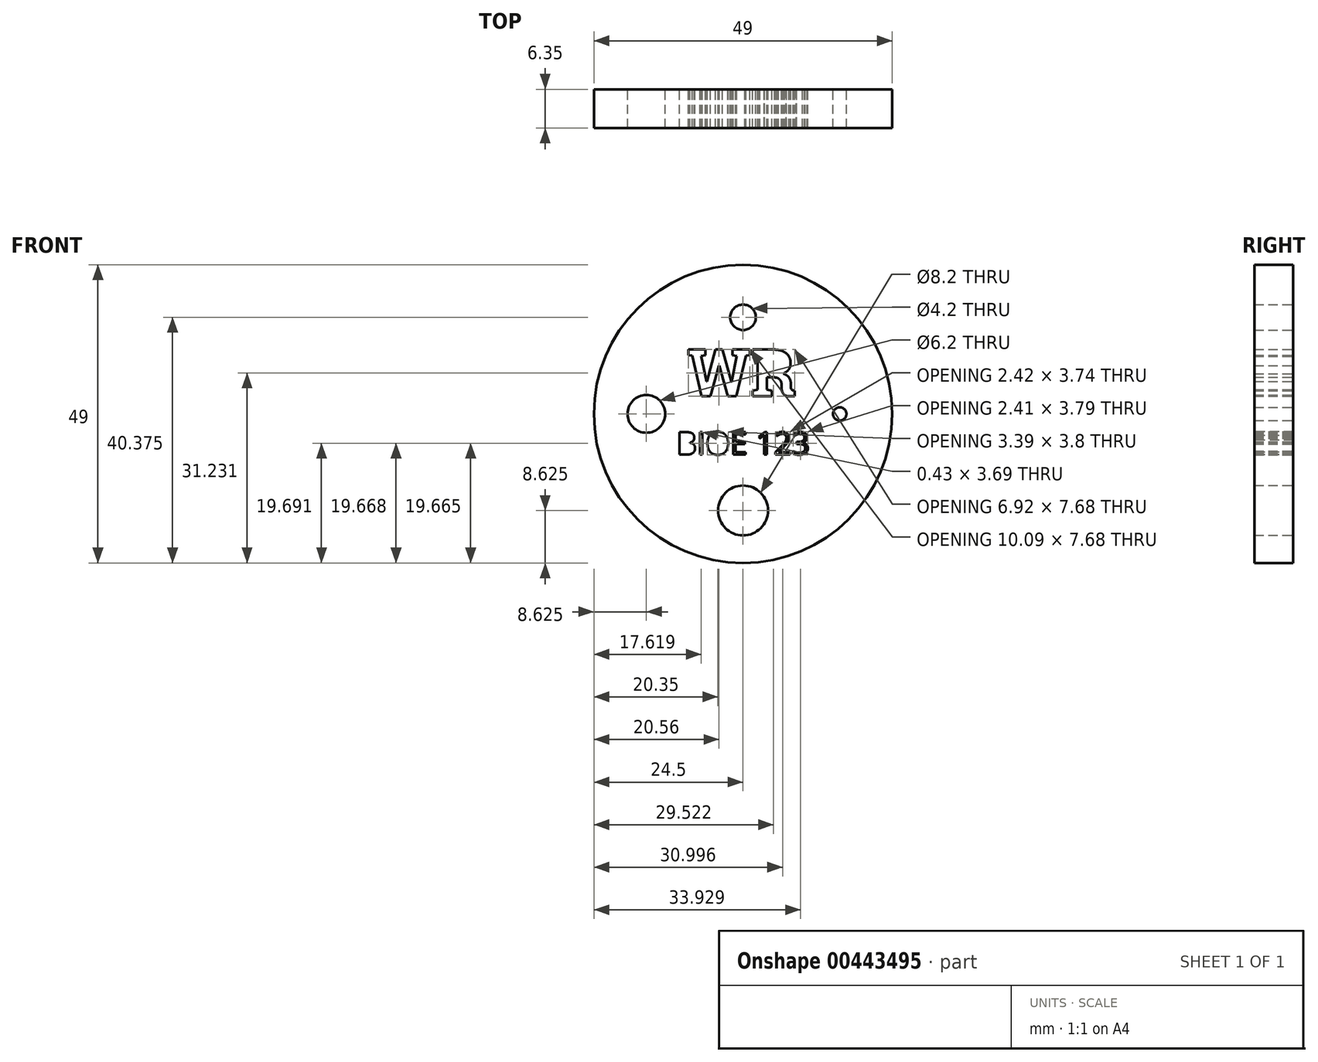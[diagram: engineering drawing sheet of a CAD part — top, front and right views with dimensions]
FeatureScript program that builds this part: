
annotation { "Feature Type Name" : "Feature", "Feature Type Description" : "" }
export const myFeature = defineFeature(function(context is Context, id is Id, definition is map)
    precondition{}
    {
        {
            var Q0;
            Q0=qCreatedBy(makeId("Front.planeOp"),FACE);
            var sketch = newSketch(context, id + "F0", { "sketchPlane" : qUnion([Q0])});
            skCircle(sketch, "E0", {"center": v(0, 0) * mm, "radius": 24.5 * mm});
            skCircle(sketch, "E1", {"center": v(-15.88, 0) * mm, "radius": 3.1 * mm});
            skCircle(sketch, "E2", {"center": v(0, 15.88) * mm, "radius": 2.1 * mm});
            skCircle(sketch, "E3", {"center": v(15.88, 0) * mm, "radius": 1.1 * mm});
            skCircle(sketch, "E4", {"center": v(0, -15.88) * mm, "radius": 4.1 * mm});
            skText(sketch, "E5", { "text": "WR\n", "fontName": "RobotoSlab-Bold.ttf"});
            skText(sketch, "E6", { "text": "BIOE 123", "fontName": "OpenSans-Regular.ttf"});
            const initialGuessF0  = {"E5": [-0.00914, 0.00289, 1, 0, 0.00778], "E6": [-0.01095, -0.00668, 1, 0, 0.00372]};
            skSetInitialGuess(sketch, initialGuessF0);
            skSolve(sketch);
        }
        {
            var Q0;
            Q0=makeQuery(id+"F0.imprint","IMPRINT",FACE,{"disambiguationData":[TD([[makeQuery(id+"F0.imprint","IMPRINT",EDGE,{"derivedFrom":sQuery(id+"F0.wireOp",EDGE,"E0")}),1.0]])]});
            extrude(context, id + "F1", {"entities" : qUnion([Q0]), "depth" : 6.35 * mm});
        }
    });
